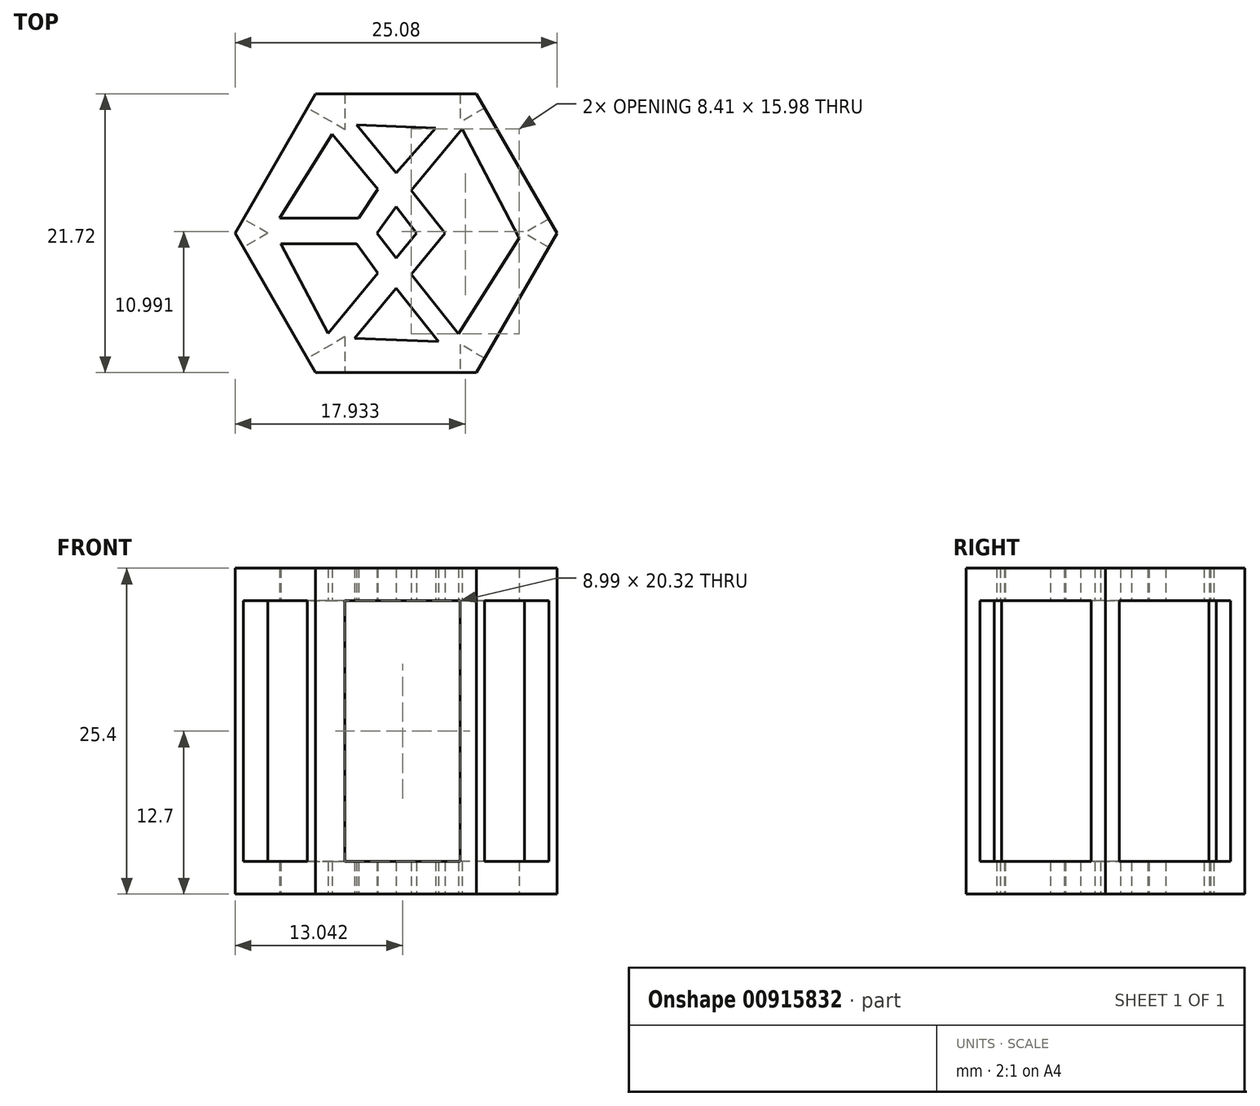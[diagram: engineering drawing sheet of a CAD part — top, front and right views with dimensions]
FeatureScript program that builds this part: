
annotation { "Feature Type Name" : "Feature", "Feature Type Description" : "" }
export const myFeature = defineFeature(function(context is Context, id is Id, definition is map)
    precondition{}
    {
        {
            var Q0;
            Q0=qCreatedBy(makeId("Top.planeOp"),FACE);
            var sketch = newSketch(context, id + "F0", { "sketchPlane" : qUnion([Q0])});
            skCircle(sketch, "E0.cCircle", {"center": v(0, 0) * mm, "radius": 10.86 * mm, "construction": true});
            skLineSegment(sketch, "E0.0", {"start": v(-6.27, 10.86) * mm, "end": v(6.27, 10.86) * mm});
            skLineSegment(sketch, "E0.1", {"start": v(6.27, 10.86) * mm, "end": v(12.54, 0) * mm});
            skLineSegment(sketch, "E0.2", {"start": v(12.54, 0) * mm, "end": v(6.27, -10.86) * mm});
            skLineSegment(sketch, "E0.3", {"start": v(6.27, -10.86) * mm, "end": v(-6.27, -10.86) * mm});
            skLineSegment(sketch, "E0.4", {"start": v(-6.27, -10.86) * mm, "end": v(-12.54, 0) * mm});
            skLineSegment(sketch, "E0.5", {"start": v(-12.54, 0) * mm, "end": v(-6.27, 10.86) * mm});
            skPoint(sketch, "E0.0.midPoint", {"position": v(0, 10.86) * mm});
            skLineSegment(sketch, "E1", {"start": v(6.27, 10.86) * mm, "end": v(-2.66, 0) * mm, "construction": true});
            skLineSegment(sketch, "E2", {"start": v(-2.66, 0) * mm, "end": v(6.27, -10.86) * mm, "construction": true});
            skLineSegment(sketch, "E3", {"start": v(-6.27, 10.86) * mm, "end": v(2.7, 0) * mm, "construction": true});
            skLineSegment(sketch, "E4", {"start": v(2.7, 0) * mm, "end": v(-6.27, -10.86) * mm, "construction": true});
            skLineSegment(sketch, "E5", {"start": v(-2.66, 0) * mm, "end": v(-12.54, 0) * mm, "construction": true});
            skCircle(sketch, "E6.cCircle", {"center": v(0, 0) * mm, "radius": 8.32 * mm, "construction": true});
            skLineSegment(sketch, "E6.0", {"start": v(-9.6, 0.38) * mm, "end": v(-4.47, 8.5) * mm, "construction": true});
            skLineSegment(sketch, "E6.1", {"start": v(-4.47, 8.5) * mm, "end": v(5.13, 8.12) * mm, "construction": true});
            skLineSegment(sketch, "E6.2", {"start": v(5.13, 8.12) * mm, "end": v(9.6, -0.38) * mm, "construction": true});
            skLineSegment(sketch, "E6.3", {"start": v(9.6, -0.38) * mm, "end": v(4.47, -8.5) * mm, "construction": true});
            skLineSegment(sketch, "E6.4", {"start": v(4.47, -8.5) * mm, "end": v(-5.13, -8.12) * mm, "construction": true});
            skLineSegment(sketch, "E6.5", {"start": v(-5.13, -8.12) * mm, "end": v(-9.6, 0.38) * mm, "construction": true});
            skPoint(sketch, "E6.0.midPoint", {"position": v(-7.03, 4.44) * mm});
            skSolve(sketch);
        }
        {
            var Q0;
            Q0=makeQuery(id+"F0.imprint","IMPRINT",FACE,{"disambiguationData":[TD([[makeQuery(id+"F0.imprint","IMPRINT",EDGE,{"derivedFrom":sQuery(id+"F0.wireOp",EDGE,"E0.0")}),-1.0]])]});
            var sketch = newSketch(context, id + "F1", { "sketchPlane" : qUnion([Q0])});
            skCircle(sketch, "E7.cCircle", {"center": v(0, 0) * mm, "radius": 8.32 * mm, "construction": true});
            skLineSegment(sketch, "E7.0", {"start": v(-4.47, 8.5) * mm, "end": v(5.13, 8.12) * mm, "construction": true});
            skLineSegment(sketch, "E7.1", {"start": v(5.13, 8.12) * mm, "end": v(9.6, -0.38) * mm, "construction": true});
            skLineSegment(sketch, "E7.2", {"start": v(9.6, -0.38) * mm, "end": v(4.47, -8.5) * mm, "construction": true});
            skLineSegment(sketch, "E7.3", {"start": v(4.47, -8.5) * mm, "end": v(-5.13, -8.12) * mm, "construction": true});
            skLineSegment(sketch, "E7.4", {"start": v(-5.13, -8.12) * mm, "end": v(-9.6, 0.38) * mm, "construction": true});
            skLineSegment(sketch, "E7.5", {"start": v(-9.6, 0.38) * mm, "end": v(-4.47, 8.5) * mm, "construction": true});
            skPoint(sketch, "E7.0.midPoint", {"position": v(0.33, 8.31) * mm});
            skLineSegment(sketch, "E8", {"start": v(5.13, 8.12) * mm, "end": v(1.19, 3.33) * mm});
            skLineSegment(sketch, "E9", {"start": v(1.19, 3.33) * mm, "end": v(3.82, 0) * mm});
            skLineSegment(sketch, "E10", {"start": v(3.82, 0) * mm, "end": v(1.19, -3.2) * mm});
            skLineSegment(sketch, "E11", {"start": v(1.19, -3.2) * mm, "end": v(4.87, -7.86) * mm});
            skLineSegment(sketch, "E12", {"start": v(0, 2.06) * mm, "end": v(-1.5, 0) * mm});
            skLineSegment(sketch, "E13", {"start": v(-1.5, 0) * mm, "end": v(0, -1.94) * mm});
            skLineSegment(sketch, "E14", {"start": v(0, -1.94) * mm, "end": v(1.59, 0) * mm});
            skLineSegment(sketch, "E15", {"start": v(1.59, 0) * mm, "end": v(0, 2.06) * mm});
            skLineSegment(sketch, "E16", {"start": v(-3.1, 8.45) * mm, "end": v(0, 4.7) * mm});
            skLineSegment(sketch, "E17", {"start": v(0, 4.7) * mm, "end": v(3.09, 8.2) * mm});
            skLineSegment(sketch, "E18", {"start": v(-4.97, 7.7) * mm, "end": v(-1.43, 3.42) * mm});
            skLineSegment(sketch, "E19", {"start": v(-1.43, -3.1) * mm, "end": v(-5.3, -7.8) * mm});
            skLineSegment(sketch, "E20", {"start": v(-3.24, -8.2) * mm, "end": v(0, -4.27) * mm});
            skLineSegment(sketch, "E21", {"start": v(0, -4.27) * mm, "end": v(3.31, -8.46) * mm});
            skLineSegment(sketch, "E22", {"start": v(-9.1, 1.18) * mm, "end": v(-2.92, 1.18) * mm});
            skLineSegment(sketch, "E23", {"start": v(-8.97, -0.81) * mm, "end": v(-3.08, -0.81) * mm});
            skLineSegment(sketch, "E24", {"start": v(-1.43, 3.42) * mm, "end": v(-2.92, 1.18) * mm});
            skLineSegment(sketch, "E25", {"start": v(-3.08, -0.81) * mm, "end": v(-1.43, -3.1) * mm});
            skLineSegment(sketch, "E26", {"start": v(-4.97, 7.7) * mm, "end": v(-9.1, 1.18) * mm});
            skLineSegment(sketch, "E27", {"start": v(-8.97, -0.81) * mm, "end": v(-5.3, -7.8) * mm});
            skLineSegment(sketch, "E28", {"start": v(-3.24, -8.2) * mm, "end": v(3.31, -8.46) * mm});
            skLineSegment(sketch, "E29", {"start": v(4.87, -7.86) * mm, "end": v(9.6, -0.38) * mm});
            skLineSegment(sketch, "E30", {"start": v(9.6, -0.38) * mm, "end": v(5.13, 8.12) * mm});
            skLineSegment(sketch, "E31", {"start": v(-3.1, 8.45) * mm, "end": v(3.09, 8.2) * mm});
            skSolve(sketch);
        }
        {
            var Q0;
            Q0=makeQuery(id+"F1.imprint","IMPRINT",FACE,{"disambiguationData":[TD([[makeQuery(id+"F1.imprint","IMPRINT",EDGE,{"derivedFrom":sQuery(id+"F1.wireOp",EDGE,"E8")}),-1.0]])]});
            extrude(context, id + "F2", {"entities" : qUnion([Q0]), "depth" : 25.4 * mm, "offsetDistance" : 25.4 * mm});
        }
        {
            var Q0;
            Q0=makeQuery(id+"F2.opExtrude","SWEPT_FACE",FACE,{"disambiguationData":[OSD([sQuery(id+"F0.wireOp",EDGE,"E0.3")])]});
            var sketch = newSketch(context, id + "F3", { "sketchPlane" : qUnion([Q0])});
            skLineSegment(sketch, "E32", {"start": v(-6.27, 21.28) * mm, "end": v(-5, 21.28) * mm, "construction": true});
            skLineSegment(sketch, "E33", {"start": v(-4, 25.4) * mm, "end": v(-4, 22.86) * mm, "construction": true});
            skLineSegment(sketch, "E34", {"start": v(-5, 21.28) * mm, "end": v(-5, 22.86) * mm});
            skLineSegment(sketch, "E35", {"start": v(-5, 22.86) * mm, "end": v(5, 22.86) * mm});
            skLineSegment(sketch, "E36", {"start": v(5, 22.86) * mm, "end": v(5, 2.54) * mm});
            skLineSegment(sketch, "E37", {"start": v(5, 2.54) * mm, "end": v(-4, 2.54) * mm});
            skLineSegment(sketch, "E38", {"start": v(-4, 2.54) * mm, "end": v(-4, 22.86) * mm});
            skLineSegment(sketch, "E39", {"start": v(0.5, 2.54) * mm, "end": v(0.5, 0) * mm, "construction": true});
            skLineSegment(sketch, "E40", {"start": v(5, 12.7) * mm, "end": v(6.27, 12.7) * mm, "construction": true});
            skSolve(sketch);
        }
        {
            var Q0;
            {var subQ0=sQuery(id+"F3.wireOp",EDGE,"E36");Q0=makeQuery(id+"F3.imprint","IMPRINT",FACE,{"disambiguationData":[TD([[makeQuery(id+"F3.imprint","IMPRINT",EDGE,{"derivedFrom":subQ0}),-1.0]])]});}
            extrude(context, id + "F4", {"entities" : qUnion([Q0]), "operationType" : NewBodyOperationType.REMOVE, "endBound" : BoundingType.THROUGH_ALL, "oppositeDirection" : true, "depth" : 44.2 * mm, "offsetDistance" : 25.4 * mm});
        }
        {
            var Q0;
            Q0=makeQuery(id+"F2.opExtrude","SWEPT_FACE",FACE,{"disambiguationData":[OSD([sQuery(id+"F0.wireOp",EDGE,"E0.4")])]});
            var sketch = newSketch(context, id + "F5", { "sketchPlane" : qUnion([Q0])});
            skLineSegment(sketch, "E41", {"start": v(0, 25.4) * mm, "end": v(0, 22.86) * mm, "construction": true});
            skLineSegment(sketch, "E42", {"start": v(-6.27, 2.54) * mm, "end": v(-5, 2.54) * mm, "construction": true});
            skLineSegment(sketch, "E43", {"start": v(-5, 2.54) * mm, "end": v(-5, 22.86) * mm});
            skLineSegment(sketch, "E44", {"start": v(0, 22.86) * mm, "end": v(-5, 22.86) * mm});
            skLineSegment(sketch, "E45", {"start": v(0, 22.86) * mm, "end": v(5, 22.86) * mm});
            skLineSegment(sketch, "E46", {"start": v(5, 22.86) * mm, "end": v(5, 2.54) * mm});
            skLineSegment(sketch, "E47", {"start": v(5, 2.54) * mm, "end": v(-5, 2.54) * mm});
            skLineSegment(sketch, "E48", {"start": v(0, 0) * mm, "end": v(0, 2.54) * mm, "construction": true});
            skLineSegment(sketch, "E49", {"start": v(5, 12.7) * mm, "end": v(6.27, 12.7) * mm, "construction": true});
            skSolve(sketch);
        }
        {
            var Q0;
            Q0=makeQuery(id+"F5.imprint","IMPRINT",FACE,{"disambiguationData":[TD([[makeQuery(id+"F5.imprint","IMPRINT",EDGE,{"derivedFrom":sQuery(id+"F5.wireOp",EDGE,"E43")}),-1.0]])]});
            extrude(context, id + "F6", {"entities" : qUnion([Q0]), "operationType" : NewBodyOperationType.REMOVE, "endBound" : BoundingType.THROUGH_ALL, "oppositeDirection" : true, "depth" : 25.4 * mm, "offsetDistance" : 25.4 * mm});
        }
        {
            var Q0;
            Q0=makeQuery(id+"F2.opExtrude","SWEPT_FACE",FACE,{"disambiguationData":[OSD([sQuery(id+"F0.wireOp",EDGE,"E0.5")])]});
            var sketch = newSketch(context, id + "F7", { "sketchPlane" : qUnion([Q0])});
            skLineSegment(sketch, "E50", {"start": v(0, 0) * mm, "end": v(0, 2.54) * mm, "construction": true});
            skLineSegment(sketch, "E51", {"start": v(-6.27, 12.7) * mm, "end": v(-5, 12.7) * mm, "construction": true});
            skLineSegment(sketch, "E52", {"start": v(6.27, 12.7) * mm, "end": v(5, 12.7) * mm, "construction": true});
            skLineSegment(sketch, "E53", {"start": v(0, 25.4) * mm, "end": v(0, 22.86) * mm, "construction": true});
            skLineSegment(sketch, "E54", {"start": v(-5, 12.7) * mm, "end": v(-5, 2.54) * mm});
            skLineSegment(sketch, "E55", {"start": v(5, 12.7) * mm, "end": v(5, 2.54) * mm});
            skLineSegment(sketch, "E56", {"start": v(5, 2.54) * mm, "end": v(-5, 2.54) * mm});
            skLineSegment(sketch, "E57", {"start": v(0, 22.86) * mm, "end": v(5, 22.86) * mm});
            skLineSegment(sketch, "E58", {"start": v(5, 22.86) * mm, "end": v(5, 12.7) * mm});
            skLineSegment(sketch, "E59", {"start": v(0, 22.86) * mm, "end": v(-5, 22.86) * mm});
            skLineSegment(sketch, "E60", {"start": v(-5, 12.7) * mm, "end": v(-5, 22.86) * mm});
            skSolve(sketch);
        }
        {
            var Q0;
            Q0=makeQuery(id+"F7.imprint","IMPRINT",FACE,{"disambiguationData":[TD([[makeQuery(id+"F7.imprint","IMPRINT",EDGE,{"derivedFrom":sQuery(id+"F7.wireOp",EDGE,"E54")}),1.0]])]});
            extrude(context, id + "F8", {"entities" : qUnion([Q0]), "operationType" : NewBodyOperationType.REMOVE, "endBound" : BoundingType.THROUGH_ALL, "oppositeDirection" : true, "depth" : 12.52 * mm, "offsetDistance" : 25.4 * mm});
        }
    });
